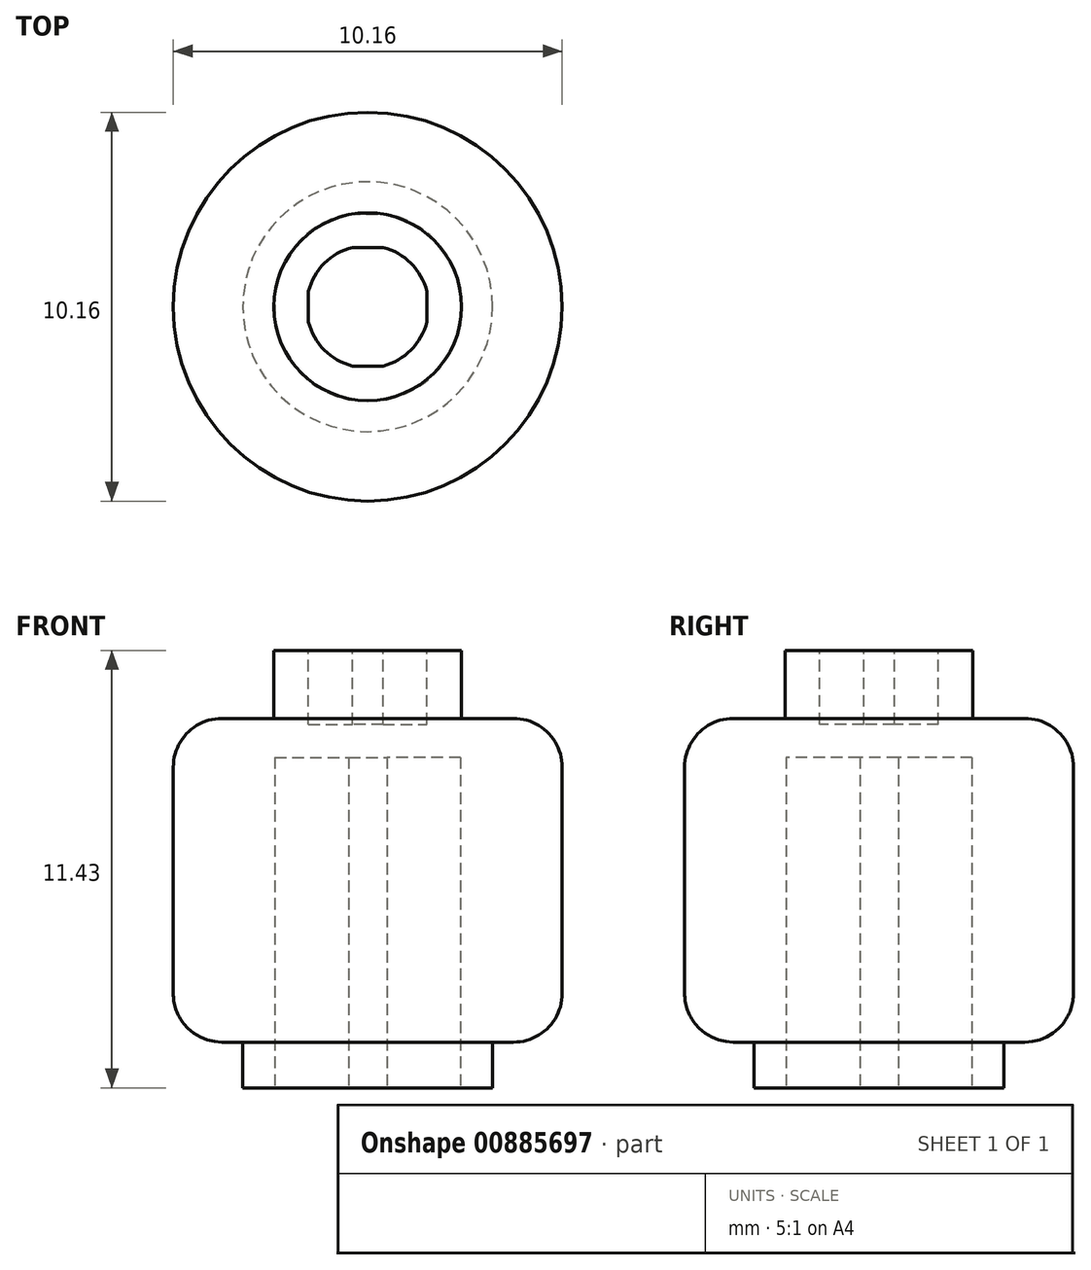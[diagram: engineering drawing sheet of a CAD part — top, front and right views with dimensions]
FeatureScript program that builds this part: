
annotation { "Feature Type Name" : "Feature", "Feature Type Description" : "" }
export const myFeature = defineFeature(function(context is Context, id is Id, definition is map)
    precondition{}
    {
        {
            var Q0;
            Q0=qCreatedBy(makeId("Right.planeOp"),FACE);
            var sketch = newSketch(context, id + "F0", { "sketchPlane" : qUnion([Q0])});
            skLineSegment(sketch, "E0", {"start": v(2.48, 0) * mm, "end": v(2.48, 8.64) * mm});
            skLineSegment(sketch, "E1", {"start": v(2.48, 8.64) * mm, "end": v(0, 8.64) * mm});
            skLineSegment(sketch, "E2", {"start": v(0, 8.64) * mm, "end": v(0, 9.5) * mm});
            skLineSegment(sketch, "E3", {"start": v(0, 9.5) * mm, "end": v(1.6, 9.5) * mm});
            skLineSegment(sketch, "E4", {"start": v(1.6, 9.5) * mm, "end": v(1.6, 11.43) * mm});
            skLineSegment(sketch, "E5", {"start": v(1.6, 11.43) * mm, "end": v(2.45, 11.43) * mm});
            skLineSegment(sketch, "E6", {"start": v(2.45, 11.43) * mm, "end": v(2.45, 9.65) * mm});
            skLineSegment(sketch, "E7", {"start": v(2.45, 9.65) * mm, "end": v(3.8, 9.65) * mm});
            skLineSegment(sketch, "E8", {"start": v(2.48, 0) * mm, "end": v(3.26, 0) * mm});
            skLineSegment(sketch, "E9", {"start": v(3.26, 0) * mm, "end": v(3.26, 1.2) * mm});
            skLineSegment(sketch, "E10", {"start": v(3.26, 1.2) * mm, "end": v(3.81, 1.2) * mm});
            skLineSegment(sketch, "E11", {"start": v(5.08, 2.46) * mm, "end": v(5.08, 8.38) * mm});
            skArc(sketch, "E12", {"start": v(5.08, 8.38) * mm, "mid": v(4.7, 9.28) * mm, "end": v(3.8, 9.65) * mm});
            skArc(sketch, "E13", {"start": v(3.81, 1.2) * mm, "mid": v(4.7, 1.57) * mm, "end": v(5.08, 2.46) * mm});
            skLineSegment(sketch, "E14", {"start": v(0, 8.64) * mm, "end": v(0, 0) * mm, "construction": true});
            skSolve(sketch);
        }
        {
            var Q0;
            Q0 = qSketchRegion(id + "F0", true);
            var Q1;
            Q1=sQuery(id+"F0.wireOp",EDGE,"E14");
            revolve(context, id + "F1", {"surfaceOperationType" : NewSurfaceOperationType.NEW, "entities" : qUnion([Q0]), "axis" : qUnion([Q1]), "revolveType" : RevolveType.FULL});
        }
        {
            var Q0;
            Q0=makeQuery(id+"F1.opRevolve","SWEPT_FACE",FACE,{"disambiguationData":[OSD([sQuery(id+"F0.wireOp",EDGE,"E8")])]});
            var sketch = newSketch(context, id + "F2", { "sketchPlane" : qUnion([Q0])});
            skLineSegment(sketch, "E15.bottom", {"start": v(0.5, 2.43) * mm, "end": v(-0.5, 2.43) * mm});
            skLineSegment(sketch, "E15.top", {"start": v(0.5, 2.48) * mm, "end": v(-0.5, 2.48) * mm});
            skLineSegment(sketch, "E15.left", {"start": v(0.5, 2.43) * mm, "end": v(0.5, 2.48) * mm});
            skLineSegment(sketch, "E15.right", {"start": v(-0.5, 2.43) * mm, "end": v(-0.5, 2.48) * mm});
            skLineSegment(sketch, "E16.bottom", {"start": v(2.43, 0.5) * mm, "end": v(2.48, 0.5) * mm});
            skLineSegment(sketch, "E16.top", {"start": v(2.43, -0.5) * mm, "end": v(2.48, -0.5) * mm});
            skLineSegment(sketch, "E16.left", {"start": v(2.43, 0.5) * mm, "end": v(2.43, -0.5) * mm});
            skLineSegment(sketch, "E16.right", {"start": v(2.48, 0.5) * mm, "end": v(2.48, -0.5) * mm});
            skLineSegment(sketch, "E17.bottom", {"start": v(0.5, -2.43) * mm, "end": v(-0.5, -2.43) * mm});
            skLineSegment(sketch, "E17.top", {"start": v(0.5, -2.48) * mm, "end": v(-0.5, -2.48) * mm});
            skLineSegment(sketch, "E17.left", {"start": v(0.5, -2.43) * mm, "end": v(0.5, -2.48) * mm});
            skLineSegment(sketch, "E17.right", {"start": v(-0.5, -2.43) * mm, "end": v(-0.5, -2.48) * mm});
            skLineSegment(sketch, "E18.bottom", {"start": v(-2.43, 0.5) * mm, "end": v(-2.48, 0.5) * mm});
            skLineSegment(sketch, "E18.top", {"start": v(-2.43, -0.5) * mm, "end": v(-2.48, -0.5) * mm});
            skLineSegment(sketch, "E18.left", {"start": v(-2.43, 0.5) * mm, "end": v(-2.43, -0.5) * mm});
            skLineSegment(sketch, "E18.right", {"start": v(-2.48, 0.5) * mm, "end": v(-2.48, -0.5) * mm});
            skSolve(sketch);
        }
        {
            var Q0;
            Q0 = qSketchRegion(id + "F2", true);
            var Q1;
            Q1=makeQuery(id+"F1.opRevolve","SWEPT_FACE",FACE,{"disambiguationData":[OSD([sQuery(id+"F0.wireOp",EDGE,"E1")])]});
            extrude(context, id + "F3", {"entities" : qUnion([Q0]), "operationType" : NewBodyOperationType.ADD, "endBound" : BoundingType.UP_TO_SURFACE, "oppositeDirection" : true, "depth" : 25.4 * mm, "endBoundEntityFace" : qUnion([Q1]), "offsetDistance" : 25.4 * mm});
        }
        {
            var Q0;
            Q0=makeQuery(id+"F1.opRevolve","SWEPT_FACE",FACE,{"disambiguationData":[OSD([sQuery(id+"F0.wireOp",EDGE,"E5")])]});
            var sketch = newSketch(context, id + "F4", { "sketchPlane" : qUnion([Q0])});
            skLineSegment(sketch, "E19.bottom", {"start": v(-0.4, -1.55) * mm, "end": v(0.4, -1.55) * mm});
            skLineSegment(sketch, "E19.top", {"start": v(-0.4, -1.6) * mm, "end": v(0.4, -1.6) * mm});
            skLineSegment(sketch, "E19.left", {"start": v(-0.4, -1.55) * mm, "end": v(-0.4, -1.6) * mm});
            skLineSegment(sketch, "E19.right", {"start": v(0.4, -1.55) * mm, "end": v(0.4, -1.6) * mm});
            skLineSegment(sketch, "E20.bottom", {"start": v(-1.55, -0.4) * mm, "end": v(-1.6, -0.4) * mm});
            skLineSegment(sketch, "E20.top", {"start": v(-1.55, 0.4) * mm, "end": v(-1.6, 0.4) * mm});
            skLineSegment(sketch, "E20.left", {"start": v(-1.55, -0.4) * mm, "end": v(-1.55, 0.4) * mm});
            skLineSegment(sketch, "E20.right", {"start": v(-1.6, -0.4) * mm, "end": v(-1.6, 0.4) * mm});
            skLineSegment(sketch, "E21.bottom", {"start": v(-0.4, 1.55) * mm, "end": v(0.4, 1.55) * mm});
            skLineSegment(sketch, "E21.top", {"start": v(-0.4, 1.6) * mm, "end": v(0.4, 1.6) * mm});
            skLineSegment(sketch, "E21.left", {"start": v(-0.4, 1.55) * mm, "end": v(-0.4, 1.6) * mm});
            skLineSegment(sketch, "E21.right", {"start": v(0.4, 1.55) * mm, "end": v(0.4, 1.6) * mm});
            skLineSegment(sketch, "E22.bottom", {"start": v(1.55, -0.4) * mm, "end": v(1.6, -0.4) * mm});
            skLineSegment(sketch, "E22.top", {"start": v(1.55, 0.4) * mm, "end": v(1.6, 0.4) * mm});
            skLineSegment(sketch, "E22.left", {"start": v(1.55, -0.4) * mm, "end": v(1.55, 0.4) * mm});
            skLineSegment(sketch, "E22.right", {"start": v(1.6, -0.4) * mm, "end": v(1.6, 0.4) * mm});
            skSolve(sketch);
        }
        {
            var Q0;
            Q0 = qSketchRegion(id + "F4", true);
            var Q1;
            Q1=makeQuery(id+"F1.opRevolve","SWEPT_FACE",FACE,{"disambiguationData":[OSD([sQuery(id+"F0.wireOp",EDGE,"E3")])]});
            extrude(context, id + "F5", {"entities" : qUnion([Q0]), "operationType" : NewBodyOperationType.ADD, "endBound" : BoundingType.UP_TO_SURFACE, "oppositeDirection" : true, "depth" : 25.4 * mm, "endBoundEntityFace" : qUnion([Q1]), "offsetDistance" : 25.4 * mm});
        }
    });
